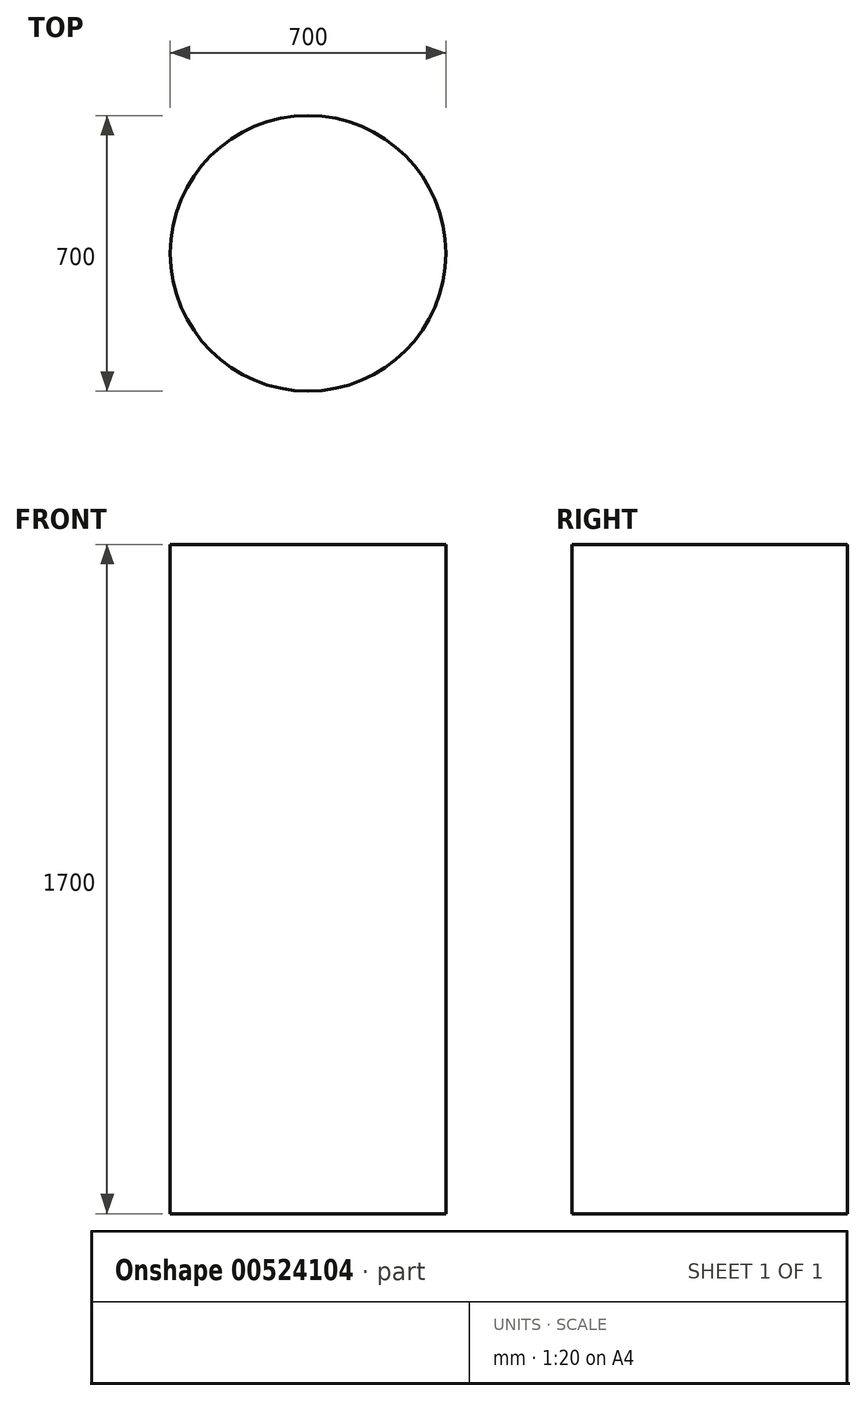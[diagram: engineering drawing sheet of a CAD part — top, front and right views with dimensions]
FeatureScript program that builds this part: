
annotation { "Feature Type Name" : "Feature", "Feature Type Description" : "" }
export const myFeature = defineFeature(function(context is Context, id is Id, definition is map)
    precondition{}
    {
        {
            var Q0;
            Q0=qCreatedBy(makeId("Top.planeOp"),FACE);
            var sketch = newSketch(context, id + "F0", { "sketchPlane" : qUnion([Q0])});
            skCircle(sketch, "E0", {"center": v(0, 0) * mm, "radius": 350 * mm});
            skSolve(sketch);
        }
        {
            var Q0;
            Q0=makeQuery(id+"F0.imprint","IMPRINT",FACE,{"disambiguationData":[TD([[makeQuery(id+"F0.imprint","IMPRINT",EDGE,{"derivedFrom":sQuery(id+"F0.wireOp",EDGE,"E0")}),1.0]])]});
            extrude(context, id + "F1", {"entities" : qUnion([Q0]), "depth" : 1700 * mm, "offsetDistance" : 25 * mm});
        }
    });
